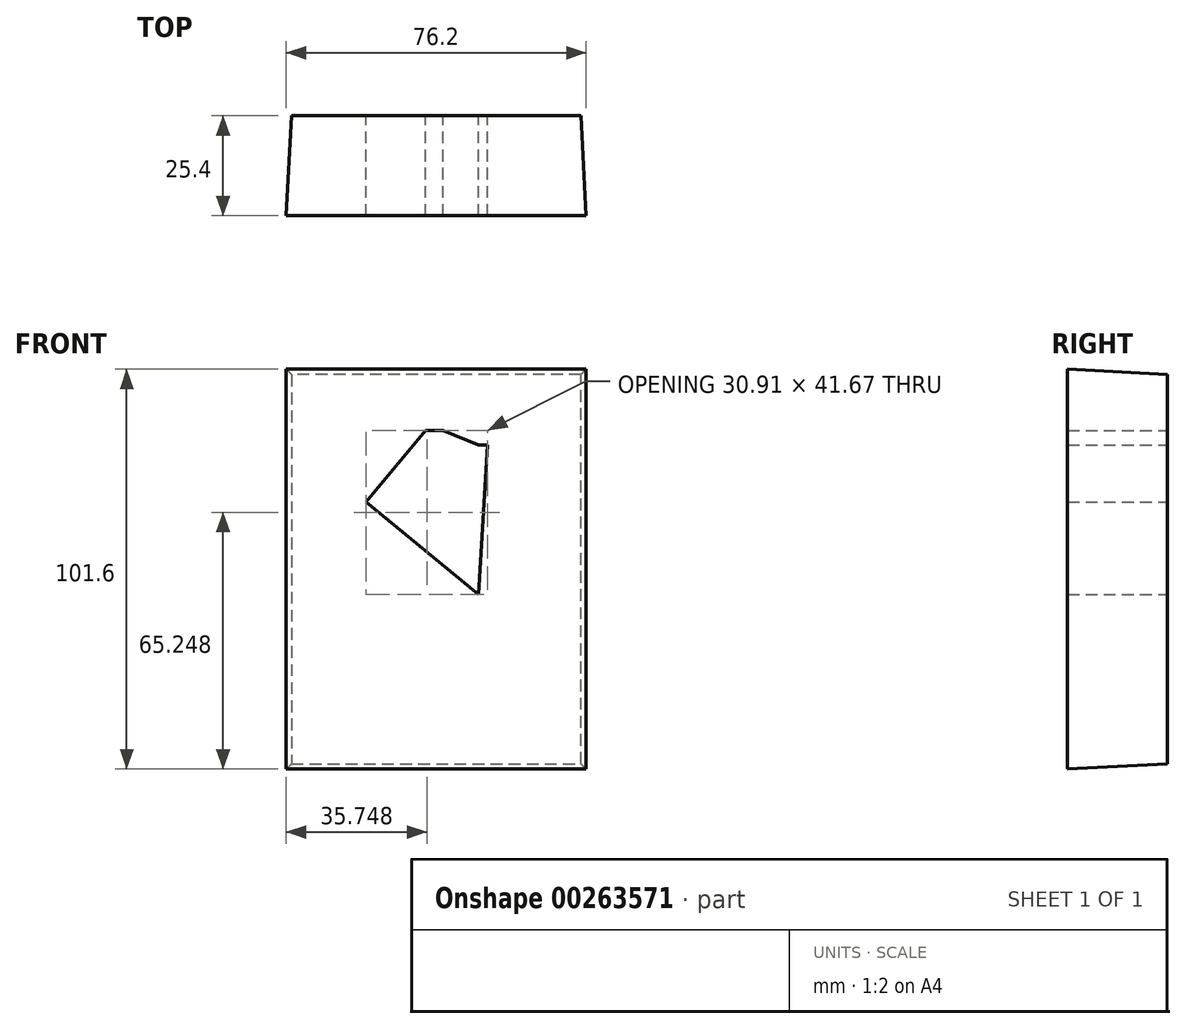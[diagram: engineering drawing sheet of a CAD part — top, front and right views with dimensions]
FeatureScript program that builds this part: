
annotation { "Feature Type Name" : "Feature", "Feature Type Description" : "" }
export const myFeature = defineFeature(function(context is Context, id is Id, definition is map)
    precondition{}
    {
        {
            var Q0;
            Q0=qCreatedBy(makeId("Front.planeOp"),FACE);
            var sketch = newSketch(context, id + "F0", { "sketchPlane" : qUnion([Q0])});
            skLineSegment(sketch, "E0.bottom", {"start": v(0, 101.6) * mm, "end": v(76.2, 101.6) * mm});
            skLineSegment(sketch, "E0.top", {"start": v(0, 0) * mm, "end": v(76.2, 0) * mm});
            skLineSegment(sketch, "E0.left", {"start": v(0, 101.6) * mm, "end": v(0, 0) * mm});
            skLineSegment(sketch, "E0.right", {"start": v(76.2, 101.6) * mm, "end": v(76.2, 0) * mm});
            skSolve(sketch);
        }
        {
            var Q0;
            Q0=makeQuery(id+"F0.imprint","IMPRINT",FACE,{"disambiguationData":[TD([[makeQuery(id+"F0.imprint","IMPRINT",EDGE,{"derivedFrom":sQuery(id+"F0.wireOp",EDGE,"E0.bottom")}),-1.0]])]});
            extrude(context, id + "F1", {"entities" : qUnion([Q0]), "oppositeDirection" : true, "depth" : 25.4 * mm, "hasDraft" : true, "draftAngle" : 3 * degree, "draftPullDirection" : true});
        }
        {
            var Q0;
            Q0=makeQuery(id+"F1.opExtrude","CAP_FACE",FACE,{"disambiguationData":[OSD([sQuery(id+"F0.wireOp",EDGE,"E0.bottom"),sQuery(id+"F0.wireOp",EDGE,"E0.top"),sQuery(id+"F0.wireOp",EDGE,"E0.left"),sQuery(id+"F0.wireOp",EDGE,"E0.right")])],"isStart":false});
            var sketch = newSketch(context, id + "F2", { "sketchPlane" : qUnion([Q0])});
            skLineSegment(sketch, "E1", {"start": v(-48.85, 44.42) * mm, "end": v(-20.3, 67.94) * mm});
            skLineSegment(sketch, "E2", {"start": v(-51.2, 82.38) * mm, "end": v(-48.85, 44.42) * mm});
            skLineSegment(sketch, "E3", {"start": v(-48.85, 82.38) * mm, "end": v(-39.78, 86.08) * mm});
            skLineSegment(sketch, "E4", {"start": v(-48.85, 82.38) * mm, "end": v(-51.2, 82.38) * mm});
            skLineSegment(sketch, "E5", {"start": v(-35.41, 86.08) * mm, "end": v(-20.3, 67.94) * mm});
            skLineSegment(sketch, "E6", {"start": v(-35.41, 86.08) * mm, "end": v(-39.78, 86.08) * mm});
            skLineSegment(sketch, "E7", {"start": v(-39.78, 86.08) * mm, "end": v(-35.41, 86.08) * mm});
            skSolve(sketch);
        }
        {
            var Q0;
            Q0=makeQuery(id+"F2.imprint","IMPRINT",FACE,{"disambiguationData":[TD([[makeQuery(id+"F2.imprint","IMPRINT",EDGE,{"derivedFrom":sQuery(id+"F2.wireOp",EDGE,"E1")}),1.0]])]});
            extrude(context, id + "F3", {"entities" : qUnion([Q0]), "operationType" : NewBodyOperationType.REMOVE, "endBound" : BoundingType.UP_TO_NEXT, "oppositeDirection" : true, "depth" : 25.4 * mm});
        }
    });
